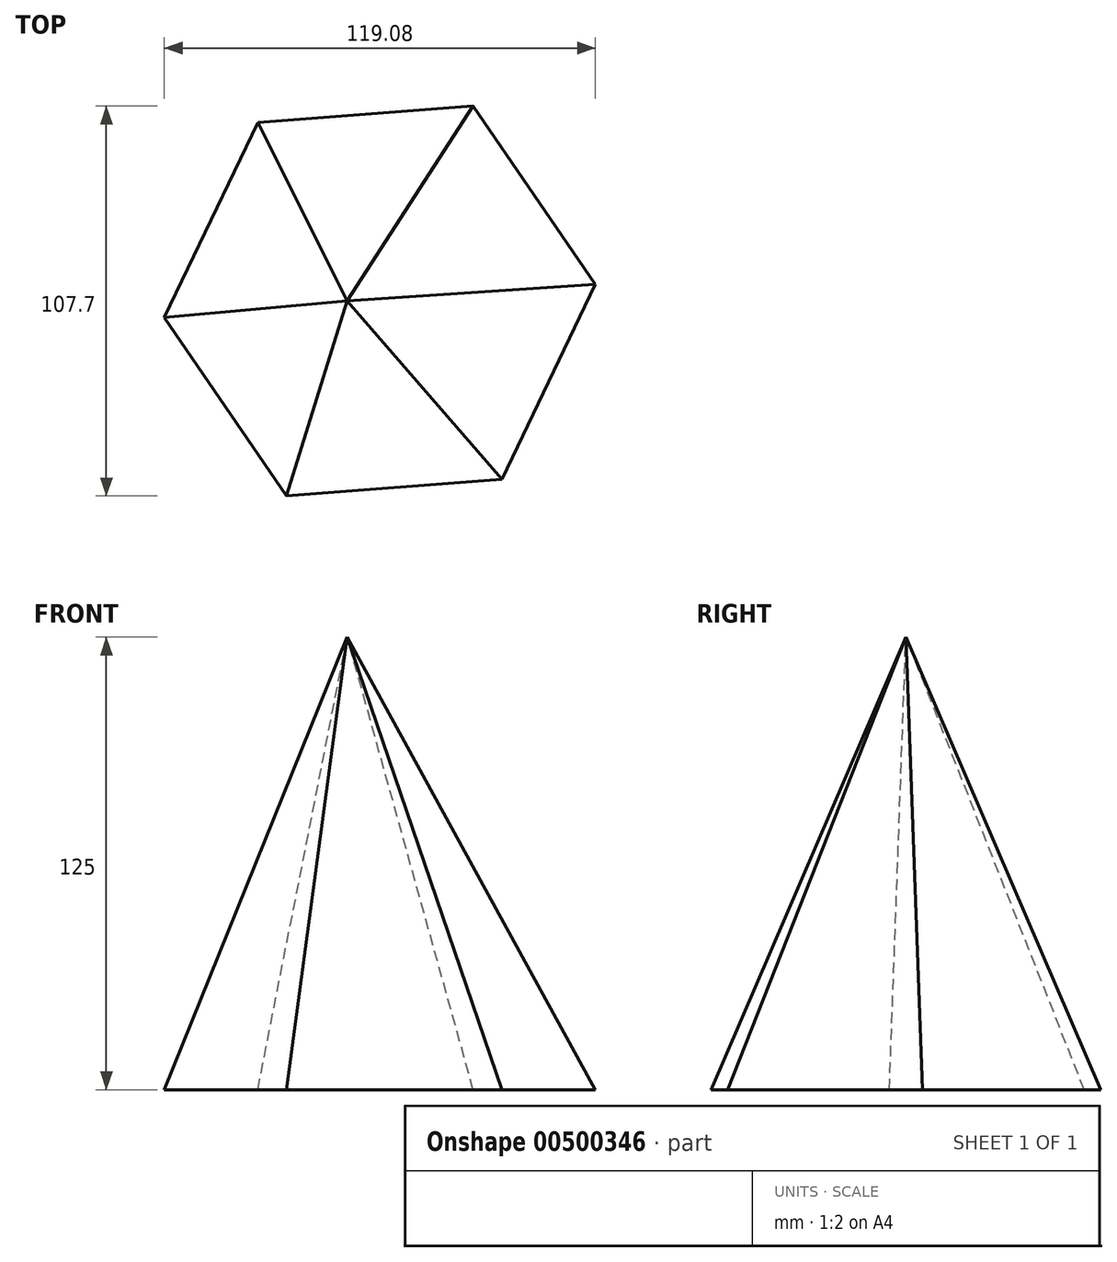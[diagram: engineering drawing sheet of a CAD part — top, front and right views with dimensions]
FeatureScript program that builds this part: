
annotation { "Feature Type Name" : "Feature", "Feature Type Description" : "" }
export const myFeature = defineFeature(function(context is Context, id is Id, definition is map)
    precondition{}
    {
        {
            var Q0;
            Q0=qCreatedBy(makeId("Top.planeOp"),FACE);
            var sketch = newSketch(context, id + "F0", { "sketchPlane" : qUnion([Q0])});
            skCircle(sketch, "E0.cCircle", {"center": v(3, 0) * mm, "radius": 59.71 * mm, "construction": true});
            skLineSegment(sketch, "E0.0", {"start": v(-22.8, -53.85) * mm, "end": v(-56.54, -4.58) * mm});
            skLineSegment(sketch, "E0.1", {"start": v(-56.54, -4.58) * mm, "end": v(-30.74, 49.27) * mm});
            skLineSegment(sketch, "E0.2", {"start": v(-30.74, 49.27) * mm, "end": v(28.8, 53.85) * mm});
            skLineSegment(sketch, "E0.3", {"start": v(28.8, 53.85) * mm, "end": v(62.54, 4.58) * mm});
            skLineSegment(sketch, "E0.4", {"start": v(62.54, 4.58) * mm, "end": v(36.74, -49.27) * mm});
            skLineSegment(sketch, "E0.5", {"start": v(36.74, -49.27) * mm, "end": v(-22.8, -53.85) * mm});
            skSolve(sketch);
        }
        {
            var Q0;
            Q0=qCreatedBy(makeId("Top.planeOp"),FACE);
            cPlane(context, id + "F1", {"entities" : qUnion([Q0]), "cplaneType" : CPlaneType.OFFSET, "offset" : 125 * mm, "width" : 150 * mm, "height" : 150 * mm});
        }
        {
            var Q0;
            Q0=qCreatedBy(id+"F1.planeOp",FACE);
            var sketch = newSketch(context, id + "F2", { "sketchPlane" : qUnion([Q0])});
            skPoint(sketch, "E1", {"position": v(-6, 0) * mm});
            skSolve(sketch);
        }
        {
            var Q0;
            Q0=makeQuery(id+"F0.imprint","IMPRINT",FACE,{"disambiguationData":[TD([[makeQuery(id+"F0.imprint","IMPRINT",EDGE,{"derivedFrom":sQuery(id+"F0.wireOp",EDGE,"E0.0")}),-1.0]])]});
            var Q1;
            Q1=sQuery(id+"F2.wireOp",VERTEX,"E1");
            loft(context, id + "F3", {"sheetProfilesArray" : [{ "sheetProfileEntities" : qUnion([Q0]) }, { "sheetProfileEntities" : qUnion([Q1]) }]});
        }
    });
